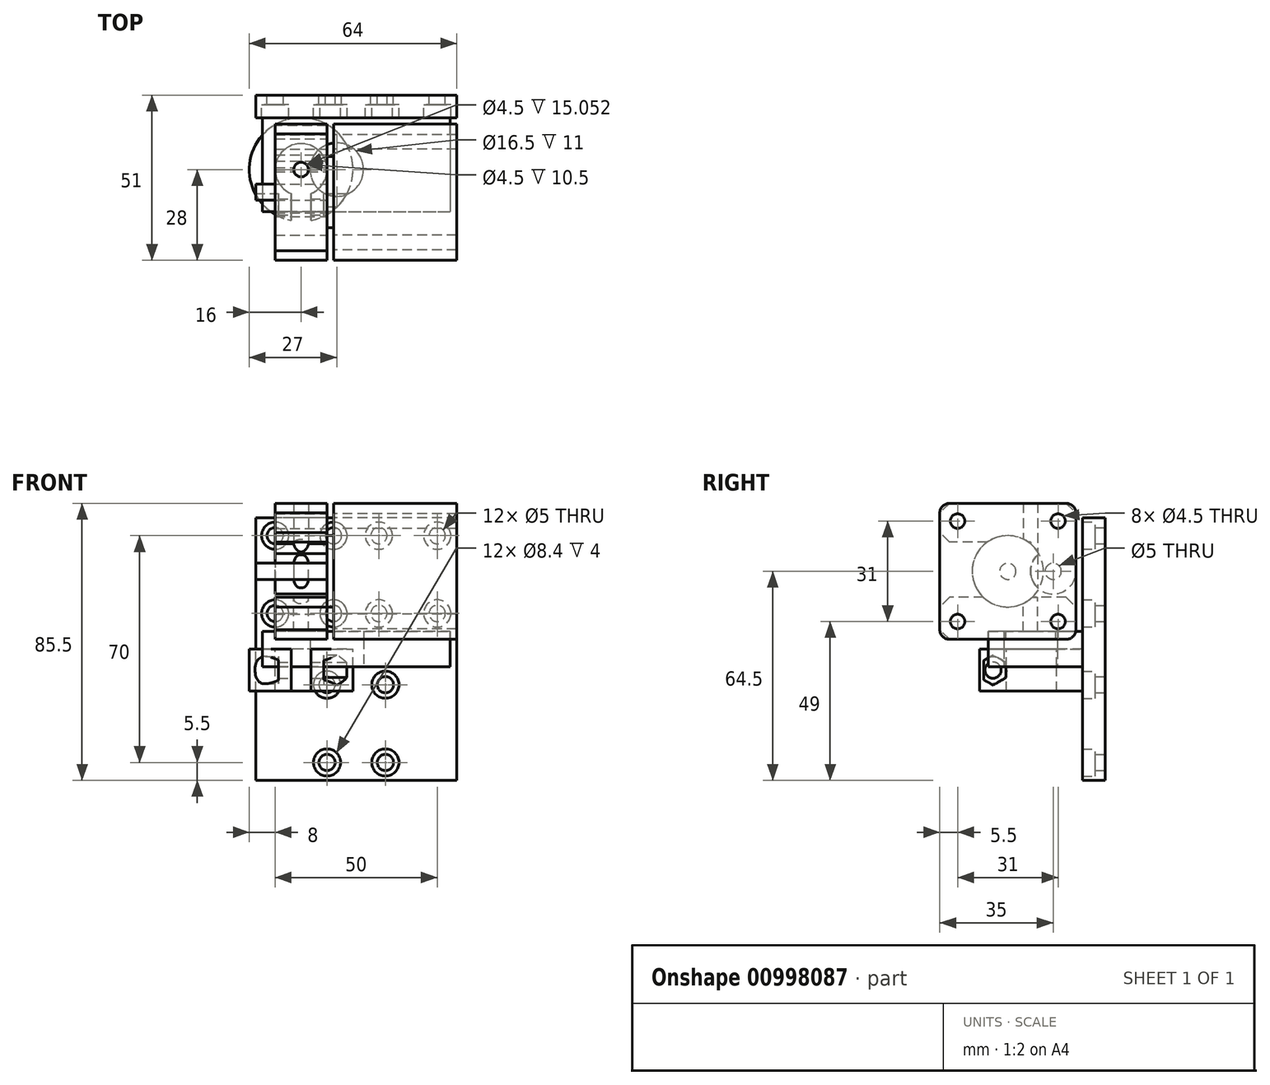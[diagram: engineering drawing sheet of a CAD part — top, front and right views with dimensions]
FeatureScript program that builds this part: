
annotation { "Feature Type Name" : "Feature", "Feature Type Description" : "" }
export const myFeature = defineFeature(function(context is Context, id is Id, definition is map)
    precondition{}
    {
        {
            var Q0;
            Q0=qCreatedBy(makeId("Front.planeOp"),FACE);
            var sketch = newSketch(context, id + "F0", { "sketchPlane" : qUnion([Q0])});
            skLineSegment(sketch, "E0.bottom", {"start": v(31, -40.5) * mm, "end": v(-31, -40.5) * mm});
            skLineSegment(sketch, "E0.top", {"start": v(31, 40.5) * mm, "end": v(-31, 40.5) * mm});
            skLineSegment(sketch, "E0.left", {"start": v(31, -40.5) * mm, "end": v(31, 40.5) * mm});
            skLineSegment(sketch, "E0.right", {"start": v(-31, -40.5) * mm, "end": v(-31, 40.5) * mm});
            skPoint(sketch, "E0.middle", {"position": v(0, 0) * mm});
            skLineSegment(sketch, "E1.bottom", {"start": v(-25, 35) * mm, "end": v(-7, 35) * mm, "construction": true});
            skLineSegment(sketch, "E1.top", {"start": v(-25, 11) * mm, "end": v(-7, 11) * mm, "construction": true});
            skLineSegment(sketch, "E1.left", {"start": v(-25, 35) * mm, "end": v(-25, 11) * mm, "construction": true});
            skLineSegment(sketch, "E1.right", {"start": v(-7, 35) * mm, "end": v(-7, 11) * mm, "construction": true});
            skLineSegment(sketch, "E2.bottom", {"start": v(-9, -11) * mm, "end": v(0, -11) * mm, "construction": true});
            skLineSegment(sketch, "E2.top", {"start": v(-9, -35) * mm, "end": v(0, -35) * mm, "construction": true});
            skLineSegment(sketch, "E2.left", {"start": v(-9, -11) * mm, "end": v(-9, -35) * mm, "construction": true});
            skLineSegment(sketch, "E3", {"start": v(0, 45.04) * mm, "end": v(0, -46.53) * mm, "construction": true});
            skCircle(sketch, "E4", {"center": v(-7, 11) * mm, "radius": 2.5 * mm});
            skCircle(sketch, "E5", {"center": v(-7, 35) * mm, "radius": 2.5 * mm});
            skCircle(sketch, "E6", {"center": v(-25, 35) * mm, "radius": 2.5 * mm});
            skCircle(sketch, "E7", {"center": v(-25, 11) * mm, "radius": 2.5 * mm});
            skCircle(sketch, "E8", {"center": v(-9, -11) * mm, "radius": 2.5 * mm});
            skCircle(sketch, "E9", {"center": v(-9, -35) * mm, "radius": 2.5 * mm});
            skCircle(sketch, "E10.MirrorC", {"center": v(7, 35) * mm, "radius": 2.5 * mm});
            skCircle(sketch, "E11.MirrorC", {"center": v(25, 35) * mm, "radius": 2.5 * mm});
            skCircle(sketch, "E12.MirrorC", {"center": v(25, 11) * mm, "radius": 2.5 * mm});
            skCircle(sketch, "E13.MirrorC", {"center": v(7, 11) * mm, "radius": 2.5 * mm});
            skCircle(sketch, "E14.MirrorC", {"center": v(9, -11) * mm, "radius": 2.5 * mm});
            skCircle(sketch, "E15.MirrorC", {"center": v(9, -35) * mm, "radius": 2.5 * mm});
            skSolve(sketch);
        }
        {
            var Q0;
            Q0 = qSketchRegion(id + "F0", true);
            extrude(context, id + "F1", {"entities" : qUnion([Q0]), "depth" : 3 * mm, "offsetDistance" : 25 * mm});
        }
        {
            var Q0;
            Q0=qCreatedBy(makeId("Top.planeOp"),FACE);
            var sketch = newSketch(context, id + "F2", { "sketchPlane" : qUnion([Q0])});
            skCircle(sketch, "E16", {"center": v(-17, -23) * mm, "radius": 8 * mm});
            skCircle(sketch, "E17", {"center": v(-17, -23) * mm, "radius": 16 * mm});
            skLineSegment(sketch, "E18", {"start": v(-17, 15.9) * mm, "end": v(-17, -56.42) * mm, "construction": true});
            skSolve(sketch);
        }
        {
            var Q0;
            Q0=qCreatedBy(makeId("Right.planeOp"),FACE);
            var Q1;
            Q1=sQuery(id+"F2.wireOp",VERTEX,"E16.center");
            cPlane(context, id + "F3", {"entities" : qUnion([Q0, Q1]), "cplaneType" : CPlaneType.PLANE_POINT, "offset" : 25 * mm, "width" : 150 * mm, "height" : 150 * mm});
        }
        {
            var Q0;
            Q0 = qSketchRegion(id + "F2", true);
            extrude(context, id + "F4", {"entities" : qUnion([Q0]), "oppositeDirection" : true, "depth" : 13 * mm, "offsetDistance" : 25 * mm});
        }
        {
            var Q0;
            Q0=makeQuery(id+"F4.opExtrude","CAP_FACE",FACE,{"disambiguationData":[OSD([sQuery(id+"F2.wireOp",EDGE,"E16"),sQuery(id+"F2.wireOp",EDGE,"E17")])],"isStart":true});
            var sketch = newSketch(context, id + "F5", { "sketchPlane" : qUnion([Q0])});
            skCircle(sketch, "E19.0", {"center": v(-17, -23) * mm, "radius": 16 * mm});
            skLineSegment(sketch, "E20.0", {"start": v(-17, 15.9) * mm, "end": v(-17, -56.42) * mm, "construction": true});
            skLineSegment(sketch, "E21", {"start": v(-20, -30.42) * mm, "end": v(-20, -38.72) * mm});
            skLineSegment(sketch, "E22.MirrorCS", {"start": v(-14, -30.42) * mm, "end": v(-14, -38.72) * mm});
            skCircle(sketch, "E23.0", {"center": v(-17, -23) * mm, "radius": 8 * mm});
            skSolve(sketch);
        }
        {
            var Q0;
            {var subQ0=sQuery(id+"F5.wireOp",EDGE,"E21");Q0=makeQuery(id+"F5.imprint","IMPRINT",FACE,{"disambiguationData":[TD([[makeQuery(id+"F5.imprint","IMPRINT",EDGE,{"derivedFrom":subQ0}),1.0]])]});}
            var Q1;
            Q1=makeQuery(id+"F4.opExtrude","CAP_FACE",FACE,{"disambiguationData":[OSD([sQuery(id+"F2.wireOp",EDGE,"E16"),sQuery(id+"F2.wireOp",EDGE,"E17")])],"isStart":false});
            extrude(context, id + "F6", {"entities" : qUnion([Q0]), "operationType" : NewBodyOperationType.REMOVE, "endBound" : BoundingType.UP_TO_SURFACE, "oppositeDirection" : true, "depth" : 25 * mm, "endBoundEntityFace" : qUnion([Q1]), "offsetDistance" : 25 * mm});
        }
        {
            var Q0;
            Q0=qCreatedBy(id+"F3.planeOp",FACE);
            var sketch = newSketch(context, id + "F7", { "sketchPlane" : qUnion([Q0])});
            skLineSegment(sketch, "E24.0.0", {"start": v(-38.72, -13) * mm, "end": v(-38.72, 0) * mm});
            skLineSegment(sketch, "E24.0.1", {"start": v(-38.72, 0) * mm, "end": v(-30.42, 0) * mm});
            skLineSegment(sketch, "E24.0.2", {"start": v(-30.42, 0) * mm, "end": v(-30.42, -13) * mm});
            skLineSegment(sketch, "E24.0.3", {"start": v(-30.42, -13) * mm, "end": v(-38.72, -13) * mm});
            skLineSegment(sketch, "E25", {"start": v(-30.42, 0) * mm, "end": v(-38.72, -13) * mm, "construction": true});
            skLineSegment(sketch, "E26", {"start": v(-38.72, 0) * mm, "end": v(-30.42, -13) * mm, "construction": true});
            skCircle(sketch, "E27", {"center": v(-34.57, -6.5) * mm, "radius": 2.5 * mm});
            skSolve(sketch);
        }
        {
            var Q0;
            Q0=makeQuery(id+"F7.imprint","IMPRINT",FACE,{"disambiguationData":[TD([[makeQuery(id+"F7.imprint","IMPRINT",EDGE,{"derivedFrom":sQuery(id+"F7.wireOp",EDGE,"E27")}),1.0]])]});
            extrude(context, id + "F8", {"entities" : qUnion([Q0]), "operationType" : NewBodyOperationType.REMOVE, "oppositeDirection" : true, "depth" : 14 * mm, "offsetDistance" : 25 * mm, "symmetric" : true});
        }
        {
            var Q0;
            Q0=makeQuery(id+"F8.boolean.opBoolean","COPY",FACE,{"derivedFrom":makeQuery(id+"F8.opExtrude","CAP_FACE",FACE,{"disambiguationData":[OSD([sQuery(id+"F7.wireOp",EDGE,"E27")])],"isStart":true})});
            var sketch = newSketch(context, id + "F9", { "sketchPlane" : qUnion([Q0])});
            skCircle(sketch, "E28.cCircle", {"center": v(34.57, -6.5) * mm, "radius": 4 * mm, "construction": true});
            skLineSegment(sketch, "E28.0", {"start": v(30.57, -8.8) * mm, "end": v(30.57, -4.2) * mm});
            skLineSegment(sketch, "E28.1", {"start": v(30.57, -4.2) * mm, "end": v(34.57, -1.88) * mm});
            skLineSegment(sketch, "E28.2", {"start": v(34.57, -1.88) * mm, "end": v(38.57, -4.2) * mm});
            skLineSegment(sketch, "E28.3", {"start": v(38.57, -4.2) * mm, "end": v(38.57, -8.8) * mm});
            skLineSegment(sketch, "E28.4", {"start": v(38.57, -8.8) * mm, "end": v(34.57, -11.12) * mm});
            skLineSegment(sketch, "E28.5", {"start": v(34.57, -11.12) * mm, "end": v(30.57, -8.8) * mm});
            skPoint(sketch, "E28.0.midPoint", {"position": v(30.57, -6.5) * mm});
            skCircle(sketch, "E29.0", {"center": v(34.57, -6.5) * mm, "radius": 2.5 * mm});
            skSolve(sketch);
        }
        {
            var Q0;
            Q0=makeQuery(id+"F9.imprint","IMPRINT",FACE,{"disambiguationData":[TD([[makeQuery(id+"F9.imprint","IMPRINT",EDGE,{"derivedFrom":sQuery(id+"F9.wireOp",EDGE,"E28.0")}),-1.0]])]});
            var Q1;
            Q1=makeQuery(id+"F9.imprint","IMPRINT",FACE,{"disambiguationData":[TD([[makeQuery(id+"F9.imprint","IMPRINT",EDGE,{"derivedFrom":sQuery(id+"F9.wireOp",EDGE,"E29.0")}),-1.0]])]});
            extrude(context, id + "F10", {"entities" : qUnion([Q0, Q1]), "operationType" : NewBodyOperationType.REMOVE, "oppositeDirection" : true, "depth" : 25 * mm, "offsetDistance" : 25 * mm});
        }
        {
            var Q0;
            Q0=makeQuery(id+"F8.boolean.opBoolean","COPY",FACE,{"derivedFrom":makeQuery(id+"F8.opExtrude","CAP_FACE",FACE,{"disambiguationData":[OSD([sQuery(id+"F7.wireOp",EDGE,"E27")])],"isStart":false})});
            var sketch = newSketch(context, id + "F11", { "sketchPlane" : qUnion([Q0])});
            skCircle(sketch, "E30", {"center": v(-34.57, -6.5) * mm, "radius": 4.2 * mm});
            skCircle(sketch, "E31.0", {"center": v(-34.57, -6.5) * mm, "radius": 2.5 * mm});
            skSolve(sketch);
        }
        {
            var Q0;
            Q0=makeQuery(id+"F11.imprint","IMPRINT",FACE,{"disambiguationData":[TD([[makeQuery(id+"F11.imprint","IMPRINT",EDGE,{"derivedFrom":sQuery(id+"F11.wireOp",EDGE,"E31.0")}),1.0]])]});
            var Q1;
            Q1=makeQuery(id+"F11.imprint","IMPRINT",FACE,{"disambiguationData":[TD([[makeQuery(id+"F11.imprint","IMPRINT",EDGE,{"derivedFrom":sQuery(id+"F11.wireOp",EDGE,"E30")}),1.0]])]});
            extrude(context, id + "F12", {"entities" : qUnion([Q0, Q1]), "operationType" : NewBodyOperationType.REMOVE, "oppositeDirection" : true, "depth" : 25 * mm, "offsetDistance" : 25 * mm});
        }
        {
            var Q0;
            Q0=qCreatedBy(makeId("Right.planeOp"),FACE);
            cPlane(context, id + "F13", {"entities" : qUnion([Q0]), "cplaneType" : CPlaneType.OFFSET, "offset" : 7 * mm, "oppositeDirection" : true, "width" : 150 * mm, "height" : 150 * mm});
        }
        {
            var Q0;
            Q0=qCreatedBy(id+"F13.planeOp",FACE);
            var sketch = newSketch(context, id + "F14", { "sketchPlane" : qUnion([Q0])});
            skLineSegment(sketch, "E32.bottom", {"start": v(-9, 3) * mm, "end": v(-51, 3) * mm});
            skLineSegment(sketch, "E32.top", {"start": v(-9, 45) * mm, "end": v(-51, 45) * mm});
            skLineSegment(sketch, "E32.left", {"start": v(-9, 3) * mm, "end": v(-9, 45) * mm});
            skLineSegment(sketch, "E32.right", {"start": v(-51, 3) * mm, "end": v(-51, 45) * mm});
            skLineSegment(sketch, "E33", {"start": v(-9, 45) * mm, "end": v(-51, 3) * mm, "construction": true});
            skLineSegment(sketch, "E34", {"start": v(-51, 45) * mm, "end": v(-9, 3) * mm, "construction": true});
            skCircle(sketch, "E35", {"center": v(-14.5, 39.5) * mm, "radius": 2.25 * mm});
            skLineSegment(sketch, "E36", {"start": v(-30, 45) * mm, "end": v(-30, 3) * mm, "construction": true});
            skLineSegment(sketch, "E37", {"start": v(-9, 24) * mm, "end": v(-51, 24) * mm, "construction": true});
            skCircle(sketch, "E38.MirrorC", {"center": v(-45.5, 39.5) * mm, "radius": 2.25 * mm});
            skCircle(sketch, "E39.MirrorC", {"center": v(-45.5, 8.5) * mm, "radius": 2.25 * mm});
            skCircle(sketch, "E40.MirrorC", {"center": v(-14.5, 8.5) * mm, "radius": 2.25 * mm});
            skSolve(sketch);
        }
        {
            var Q0;
            Q0=makeQuery(id+"F14.imprint","IMPRINT",FACE,{"disambiguationData":[TD([[makeQuery(id+"F14.imprint","IMPRINT",EDGE,{"derivedFrom":sQuery(id+"F14.wireOp",EDGE,"E32.bottom")}),-1.0]])]});
            extrude(context, id + "F15", {"entities" : qUnion([Q0]), "depth" : 38 * mm, "offsetDistance" : 25 * mm});
        }
        {
            var Q0;
            Q0=makeQuery(id+"F15.opExtrude","SWEPT_EDGE",EDGE,{"disambiguationData":[OSD([sQuery(id+"F14.wireOp",EDGE,"E32.top"),sQuery(id+"F14.wireOp",EDGE,"E32.left")])]});
            var Q1;
            Q1=makeQuery(id+"F15.opExtrude","SWEPT_EDGE",EDGE,{"disambiguationData":[OSD([sQuery(id+"F14.wireOp",EDGE,"E32.bottom"),sQuery(id+"F14.wireOp",EDGE,"E32.left")])]});
            var Q2;
            Q2=makeQuery(id+"F15.opExtrude","SWEPT_EDGE",EDGE,{"disambiguationData":[OSD([sQuery(id+"F14.wireOp",EDGE,"E32.top"),sQuery(id+"F14.wireOp",EDGE,"E32.right")])]});
            var Q3;
            Q3=makeQuery(id+"F15.opExtrude","SWEPT_EDGE",EDGE,{"disambiguationData":[OSD([sQuery(id+"F14.wireOp",EDGE,"E32.bottom"),sQuery(id+"F14.wireOp",EDGE,"E32.right")])]});
            fillet(context, id + "F16", {"entities" : qUnion([Q0, Q1, Q2, Q3]), "radius" : 3 * mm, "tangentPropagation" : true, "allowEdgeOverflow" : false});
        }
        {
            var Q0;
            Q0=makeQuery(id+"F15.opExtrude","CAP_FACE",FACE,{"disambiguationData":[OSD([sQuery(id+"F14.wireOp",EDGE,"E32.bottom"),sQuery(id+"F14.wireOp",EDGE,"E32.top"),sQuery(id+"F14.wireOp",EDGE,"E32.left"),sQuery(id+"F14.wireOp",EDGE,"E32.right"),sQuery(id+"F14.wireOp",EDGE,"E35"),sQuery(id+"F14.wireOp",EDGE,"E38.MirrorC"),sQuery(id+"F14.wireOp",EDGE,"E39.MirrorC"),sQuery(id+"F14.wireOp",EDGE,"E40.MirrorC")])],"isStart":true});
            var sketch = newSketch(context, id + "F17", { "sketchPlane" : qUnion([Q0])});
            skPoint(sketch, "E41.0", {"position": v(30, 24) * mm});
            skCircle(sketch, "E42", {"center": v(30, 24) * mm, "radius": 11 * mm});
            skSolve(sketch);
        }
        {
            var Q0;
            Q0=makeQuery(id+"F17.imprint","IMPRINT",FACE,{"disambiguationData":[TD([[makeQuery(id+"F17.imprint","IMPRINT",EDGE,{"derivedFrom":sQuery(id+"F17.wireOp",EDGE,"E42")}),1.0]])]});
            extrude(context, id + "F18", {"entities" : qUnion([Q0]), "operationType" : NewBodyOperationType.ADD, "depth" : 2 * mm, "offsetDistance" : 25 * mm});
        }
        {
            var Q0;
            Q0=makeQuery(id+"F18.opExtrude","CAP_FACE",FACE,{"disambiguationData":[OSD([sQuery(id+"F17.wireOp",EDGE,"E42")])],"isStart":false});
            var sketch = newSketch(context, id + "F19", { "sketchPlane" : qUnion([Q0])});
            skPoint(sketch, "E43.0", {"position": v(30, 24) * mm});
            skCircle(sketch, "E44", {"center": v(30, 24) * mm, "radius": 2.5 * mm});
            skSolve(sketch);
        }
        {
            var Q0;
            Q0 = qSketchRegion(id + "F19", true);
            extrude(context, id + "F20", {"entities" : qUnion([Q0]), "operationType" : NewBodyOperationType.ADD, "depth" : 22 * mm, "offsetDistance" : 25 * mm});
        }
        {
            var Q0;
            Q0=makeQuery(id+"F18.opExtrude","CAP_FACE",FACE,{"disambiguationData":[OSD([sQuery(id+"F17.wireOp",EDGE,"E42")])],"isStart":false});
            var sketch = newSketch(context, id + "F21", { "sketchPlane" : qUnion([Q0])});
            skCircle(sketch, "E45.0", {"center": v(14.5, 39.5) * mm, "radius": 2.25 * mm});
            skCircle(sketch, "E45.1", {"center": v(45.5, 39.5) * mm, "radius": 2.25 * mm});
            skCircle(sketch, "E45.2", {"center": v(45.5, 8.5) * mm, "radius": 2.25 * mm});
            skCircle(sketch, "E45.3", {"center": v(14.5, 8.5) * mm, "radius": 2.25 * mm});
            skCircle(sketch, "E46.0", {"center": v(30, 24) * mm, "radius": 2.5 * mm});
            skLineSegment(sketch, "E47.bottom", {"start": v(9, 45) * mm, "end": v(51, 45) * mm});
            skLineSegment(sketch, "E47.top", {"start": v(9, 33) * mm, "end": v(51, 33) * mm});
            skLineSegment(sketch, "E47.left", {"start": v(9, 45) * mm, "end": v(9, 33) * mm});
            skLineSegment(sketch, "E47.right", {"start": v(51, 45) * mm, "end": v(51, 33) * mm});
            skLineSegment(sketch, "E48.bottom", {"start": v(9, 16) * mm, "end": v(51, 16) * mm});
            skLineSegment(sketch, "E48.top", {"start": v(9, 3) * mm, "end": v(51, 3) * mm});
            skLineSegment(sketch, "E48.left", {"start": v(9, 16) * mm, "end": v(9, 3) * mm});
            skLineSegment(sketch, "E48.right", {"start": v(51, 16) * mm, "end": v(51, 3) * mm});
            skCircle(sketch, "E49", {"center": v(16, 24) * mm, "radius": 7 * mm});
            skLineSegment(sketch, "E50", {"start": v(9, 33) * mm, "end": v(9, 24) * mm});
            skLineSegment(sketch, "E51", {"start": v(23, 24) * mm, "end": v(23, 33) * mm});
            skLineSegment(sketch, "E52", {"start": v(9, 24) * mm, "end": v(23, 24) * mm, "construction": true});
            skCircle(sketch, "E53", {"center": v(16, 24) * mm, "radius": 2.5 * mm});
            skSolve(sketch);
        }
        {
            var Q0;
            Q0=makeQuery(id+"F21.imprint","IMPRINT",FACE,{"disambiguationData":[TD([[makeQuery(id+"F21.imprint","IMPRINT",EDGE,{"derivedFrom":sQuery(id+"F21.wireOp",EDGE,"E45.0")}),-1.0]])]});
            var Q1;
            Q1=makeQuery(id+"F21.imprint","IMPRINT",FACE,{"disambiguationData":[TD([[makeQuery(id+"F21.imprint","IMPRINT",EDGE,{"derivedFrom":sQuery(id+"F21.wireOp",EDGE,"E45.2")}),-1.0]])]});
            var Q2;
            {var subQ0=sQuery(id+"F21.wireOp",EDGE,"E49");var subQ1=makeQuery(id+"F21.imprint","INTERSECT",VERTEX,{"derivedFrom":[subQ0,sQuery(id+"F21.wireOp",EDGE,"E50")]});Q2=makeQuery(id+"F21.imprint","IMPRINT",FACE,{"disambiguationData":[TD([[makeQuery(id+"F21.imprint","IMPRINT",EDGE,{"disambiguationData":[TD([[subQ1,1.0]])],"derivedFrom":subQ0}),1.0]])]});}
            var Q3;
            {var subQ0=sQuery(id+"F21.wireOp",EDGE,"E49");var subQ1=makeQuery(id+"F21.imprint","INTERSECT",VERTEX,{"derivedFrom":[subQ0,sQuery(id+"F21.wireOp",EDGE,"E51")]});Q3=makeQuery(id+"F21.imprint","IMPRINT",FACE,{"disambiguationData":[TD([[makeQuery(id+"F21.imprint","IMPRINT",EDGE,{"disambiguationData":[TD([[subQ1,1.0]])],"derivedFrom":subQ0}),1.0]])]});}
            var Q4;
            {var subQ5=sQuery(id+"F21.wireOp",EDGE,"E50");Q4=makeQuery(id+"F21.imprint","IMPRINT",FACE,{"disambiguationData":[TD([[makeQuery(id+"F21.imprint","IMPRINT",EDGE,{"derivedFrom":subQ5}),1.0]])]});}
            extrude(context, id + "F22", {"entities" : qUnion([Q0, Q1, Q2, Q3, Q4]), "depth" : 16 * mm, "offsetDistance" : 25 * mm});
        }
        {
            var Q0;
            {var subQ0=sQuery(id+"F21.wireOp",EDGE,"E48.bottom");Q0=makeQuery(id+"F22.opExtrude","SWEPT_FACE",FACE,{"disambiguationData":[OSD([subQ0]),TDD([makeQuery(id+"F21.imprint","IMPRINT",EDGE,{"disambiguationData":[TD([[makeQuery(id+"F21.imprint","INTERSECT",VERTEX,{"derivedFrom":[subQ0,sQuery(id+"F21.wireOp",EDGE,"E48.left")]}),-1.0]])],"derivedFrom":subQ0})])]});}
            var sketch = newSketch(context, id + "F23", { "sketchPlane" : qUnion([Q0])});
            skCircle(sketch, "E54", {"center": v(-17, -23) * mm, "radius": 2.25 * mm});
            skLineSegment(sketch, "E55.0", {"start": v(-25, -9) * mm, "end": v(-9, -9) * mm});
            skPoint(sketch, "E56", {"position": v(-17, -9) * mm});
            skLineSegment(sketch, "E57", {"start": v(-17, -9) * mm, "end": v(-17, -38.9) * mm, "construction": true});
            skSolve(sketch);
        }
        {
            var Q0;
            {var subQ0=sQuery(id+"F23.wireOp",EDGE,"E54");var subQ1=sQuery(id+"F21.wireOp",EDGE,"E48.bottom");var subQ2=sQuery(id+"F17.wireOp",EDGE,"E42");var subQ3=makeQuery(id+"F22.opExtrude","SWEPT_EDGE",EDGE,{"disambiguationData":[OSD([subQ2,subQ1]),TDD([makeQuery(id+"F21.imprint","INTERSECT",VERTEX,{"disambiguationData":[OD(0.0)],"derivedFrom":[makeQuery(id+"F18.opExtrude","CAP_EDGE",EDGE,{"disambiguationData":[OSD([subQ2])],"isStart":false}),subQ1]})])]});var subQ4=makeQuery(id+"F23.imprint","INTERSECT",VERTEX,{"disambiguationData":[OD(0.0)],"derivedFrom":[subQ3,subQ0]});Q0=makeQuery(id+"F23.imprint","IMPRINT",FACE,{"disambiguationData":[TD([[makeQuery(id+"F23.imprint","IMPRINT",EDGE,{"disambiguationData":[TD([[subQ4,-1.0]])],"derivedFrom":subQ0}),1.0]])]});}
            var Q1;
            {var subQ0=sQuery(id+"F23.wireOp",EDGE,"E54");var subQ1=sQuery(id+"F21.wireOp",EDGE,"E48.bottom");var subQ2=sQuery(id+"F17.wireOp",EDGE,"E42");var subQ3=makeQuery(id+"F22.opExtrude","SWEPT_EDGE",EDGE,{"disambiguationData":[OSD([subQ2,subQ1]),TDD([makeQuery(id+"F21.imprint","INTERSECT",VERTEX,{"disambiguationData":[OD(0.0)],"derivedFrom":[makeQuery(id+"F18.opExtrude","CAP_EDGE",EDGE,{"disambiguationData":[OSD([subQ2])],"isStart":false}),subQ1]})])]});var subQ4=makeQuery(id+"F23.imprint","INTERSECT",VERTEX,{"disambiguationData":[OD(0.0)],"derivedFrom":[subQ3,subQ0]});Q1=makeQuery(id+"F23.imprint","IMPRINT",FACE,{"disambiguationData":[TD([[makeQuery(id+"F23.imprint","IMPRINT",EDGE,{"disambiguationData":[TD([[subQ4,1.0]])],"derivedFrom":subQ0}),1.0]])]});}
            var Q2;
            Q2=makeQuery(id+"F22.opExtrude","SWEPT_BODY",BODY,{"disambiguationData":[OSD([sQuery(id+"F17.wireOp",EDGE,"E42"),sQuery(id+"F21.wireOp",EDGE,"E45.2"),sQuery(id+"F21.wireOp",EDGE,"E45.3"),sQuery(id+"F21.wireOp",EDGE,"E48.bottom"),sQuery(id+"F21.wireOp",EDGE,"E48.top"),sQuery(id+"F21.wireOp",EDGE,"E48.left"),sQuery(id+"F21.wireOp",EDGE,"E48.right")])]});
            extrude(context, id + "F24", {"entities" : qUnion([Q0, Q1]), "operationType" : NewBodyOperationType.REMOVE, "endBound" : BoundingType.UP_TO_BODY, "oppositeDirection" : true, "depth" : 25 * mm, "endBoundEntityBody" : qUnion([Q2]), "offsetDistance" : 25 * mm});
        }
        {
            var Q0;
            Q0 = qSketchRegion(id + "F23", true);
            var Q1;
            Q1=makeQuery(id+"F22.opExtrude","SWEPT_FACE",FACE,{"disambiguationData":[OSD([sQuery(id+"F21.wireOp",EDGE,"E47.bottom")])]});
            var Q2;
            Q2=makeQuery(id+"F22.opExtrude","SWEPT_BODY",BODY,{"disambiguationData":[OSD([sQuery(id+"F17.wireOp",EDGE,"E42"),sQuery(id+"F21.wireOp",EDGE,"E45.0"),sQuery(id+"F21.wireOp",EDGE,"E45.1"),sQuery(id+"F21.wireOp",EDGE,"E47.bottom"),sQuery(id+"F21.wireOp",EDGE,"E47.top"),sQuery(id+"F21.wireOp",EDGE,"E47.left"),sQuery(id+"F21.wireOp",EDGE,"E47.right")])]});
            extrude(context, id + "F25", {"entities" : qUnion([Q0]), "operationType" : NewBodyOperationType.REMOVE, "endBound" : BoundingType.UP_TO_SURFACE, "depth" : 25 * mm, "endBoundEntityFace" : qUnion([Q1]), "endBoundEntityBody" : qUnion([Q2]), "offsetDistance" : 25 * mm});
        }
        {
            var Q0;
            Q0=makeQuery(id+"F22.opExtrude","SWEPT_EDGE",EDGE,{"disambiguationData":[OSD([sQuery(id+"F21.wireOp",EDGE,"E48.top"),sQuery(id+"F21.wireOp",EDGE,"E48.right")])]});
            var Q1;
            Q1=makeQuery(id+"F22.opExtrude","SWEPT_EDGE",EDGE,{"disambiguationData":[OSD([sQuery(id+"F21.wireOp",EDGE,"E48.top"),sQuery(id+"F21.wireOp",EDGE,"E48.left")])]});
            var Q2;
            Q2=makeQuery(id+"F22.opExtrude","SWEPT_EDGE",EDGE,{"disambiguationData":[OSD([sQuery(id+"F21.wireOp",EDGE,"E47.bottom"),sQuery(id+"F21.wireOp",EDGE,"E47.right")])]});
            var Q3;
            Q3=makeQuery(id+"F22.opExtrude","SWEPT_EDGE",EDGE,{"disambiguationData":[OSD([sQuery(id+"F21.wireOp",EDGE,"E47.bottom"),sQuery(id+"F21.wireOp",EDGE,"E47.left")])]});
            var Q4;
            Q4=makeQuery(id+"F22.opExtrude","SWEPT_EDGE",EDGE,{"disambiguationData":[OSD([sQuery(id+"F21.wireOp",EDGE,"E47.top"),sQuery(id+"F21.wireOp",EDGE,"E47.right")])]});
            var Q5;
            Q5=makeQuery(id+"F22.opExtrude","SWEPT_EDGE",EDGE,{"disambiguationData":[OSD([sQuery(id+"F21.wireOp",EDGE,"E48.bottom"),sQuery(id+"F21.wireOp",EDGE,"E48.right")])]});
            var Q6;
            Q6=makeQuery(id+"F22.opExtrude","SWEPT_EDGE",EDGE,{"disambiguationData":[OSD([sQuery(id+"F21.wireOp",EDGE,"E48.bottom"),sQuery(id+"F21.wireOp",EDGE,"E48.left")])]});
            chamfer(context, id + "F26", {"entities" : qUnion([Q0, Q1, Q2, Q3, Q4, Q5, Q6]), "width" : 3 * mm, "tangentPropagation" : true});
        }
        {
            var Q0;
            Q0=makeQuery(id+"F1.opExtrude","CAP_FACE",FACE,{"disambiguationData":[OSD([sQuery(id+"F0.wireOp",EDGE,"E0.bottom"),sQuery(id+"F0.wireOp",EDGE,"E0.top"),sQuery(id+"F0.wireOp",EDGE,"E0.left"),sQuery(id+"F0.wireOp",EDGE,"E0.right"),sQuery(id+"F0.wireOp",EDGE,"E4"),sQuery(id+"F0.wireOp",EDGE,"E5"),sQuery(id+"F0.wireOp",EDGE,"E6"),sQuery(id+"F0.wireOp",EDGE,"E7"),sQuery(id+"F0.wireOp",EDGE,"E8"),sQuery(id+"F0.wireOp",EDGE,"E9"),sQuery(id+"F0.wireOp",EDGE,"E10.MirrorC"),sQuery(id+"F0.wireOp",EDGE,"E11.MirrorC"),sQuery(id+"F0.wireOp",EDGE,"E12.MirrorC"),sQuery(id+"F0.wireOp",EDGE,"E13.MirrorC"),sQuery(id+"F0.wireOp",EDGE,"E14.MirrorC"),sQuery(id+"F0.wireOp",EDGE,"E15.MirrorC")])],"isStart":false});
            var sketch = newSketch(context, id + "F27", { "sketchPlane" : qUnion([Q0])});
            skCircle(sketch, "E58.0", {"center": v(-9, -11) * mm, "radius": 2.5 * mm});
            skCircle(sketch, "E58.1", {"center": v(9, -11) * mm, "radius": 2.5 * mm});
            skCircle(sketch, "E58.2", {"center": v(-9, -35) * mm, "radius": 2.5 * mm});
            skCircle(sketch, "E58.3", {"center": v(9, -35) * mm, "radius": 2.5 * mm});
            skLineSegment(sketch, "E58.4", {"start": v(-31, -40.5) * mm, "end": v(-31, 40.5) * mm});
            skLineSegment(sketch, "E58.5", {"start": v(31, -40.5) * mm, "end": v(-31, -40.5) * mm});
            skLineSegment(sketch, "E58.6", {"start": v(31, -40.5) * mm, "end": v(31, 40.5) * mm});
            skLineSegment(sketch, "E58.7", {"start": v(31, 40.5) * mm, "end": v(-31, 40.5) * mm});
            skCircle(sketch, "E58.8", {"center": v(-25, 35) * mm, "radius": 2.5 * mm});
            skCircle(sketch, "E58.9", {"center": v(-25, 11) * mm, "radius": 2.5 * mm});
            skCircle(sketch, "E58.10", {"center": v(-7, 35) * mm, "radius": 2.5 * mm});
            skCircle(sketch, "E58.11", {"center": v(-7, 11) * mm, "radius": 2.5 * mm});
            skCircle(sketch, "E58.12", {"center": v(7, 11) * mm, "radius": 2.5 * mm});
            skCircle(sketch, "E58.13", {"center": v(7, 35) * mm, "radius": 2.5 * mm});
            skCircle(sketch, "E58.14", {"center": v(25, 35) * mm, "radius": 2.5 * mm});
            skCircle(sketch, "E58.15", {"center": v(25, 11) * mm, "radius": 2.5 * mm});
            skCircle(sketch, "E59.0", {"center": v(-25, 35) * mm, "radius": 4.2 * mm});
            skLineSegment(sketch, "E60.0", {"start": v(0, 45.04) * mm, "end": v(0, -46.53) * mm, "construction": true});
            skCircle(sketch, "E61.0", {"center": v(-7, 35) * mm, "radius": 4.2 * mm});
            skCircle(sketch, "E62.0", {"center": v(-7, 11) * mm, "radius": 4.2 * mm});
            skCircle(sketch, "E63.0", {"center": v(-25, 11) * mm, "radius": 4.2 * mm});
            skCircle(sketch, "E64.0", {"center": v(-9, -11) * mm, "radius": 4.2 * mm});
            skCircle(sketch, "E65.0", {"center": v(-9, -35) * mm, "radius": 4.2 * mm});
            skCircle(sketch, "E66.MirrorC", {"center": v(9, -35) * mm, "radius": 4.2 * mm});
            skCircle(sketch, "E67.MirrorC", {"center": v(9, -11) * mm, "radius": 4.2 * mm});
            skCircle(sketch, "E68.MirrorC", {"center": v(7, 11) * mm, "radius": 4.2 * mm});
            skCircle(sketch, "E69.MirrorC", {"center": v(25, 11) * mm, "radius": 4.2 * mm});
            skCircle(sketch, "E70.MirrorC", {"center": v(7, 35) * mm, "radius": 4.2 * mm});
            skCircle(sketch, "E71.MirrorC", {"center": v(25, 35) * mm, "radius": 4.2 * mm});
            skSolve(sketch);
        }
        {
            var Q0;
            Q0=makeQuery(id+"F27.imprint","IMPRINT",FACE,{"disambiguationData":[TD([[makeQuery(id+"F27.imprint","IMPRINT",EDGE,{"derivedFrom":sQuery(id+"F27.wireOp",EDGE,"E58.4")}),-1.0]])]});
            extrude(context, id + "F28", {"entities" : qUnion([Q0]), "depth" : 4 * mm, "offsetDistance" : 25 * mm});
        }
        {
            var Q0;
            Q0=qCreatedBy(makeId("Top.planeOp"),FACE);
            var sketch = newSketch(context, id + "F29", { "sketchPlane" : qUnion([Q0])});
            skLineSegment(sketch, "E72.bottom", {"start": v(-29, -3) * mm, "end": v(29, -3) * mm});
            skLineSegment(sketch, "E72.top", {"start": v(-29, -36) * mm, "end": v(29, -36) * mm});
            skLineSegment(sketch, "E72.left", {"start": v(-29, -3) * mm, "end": v(-29, -36) * mm});
            skLineSegment(sketch, "E72.right", {"start": v(29, -3) * mm, "end": v(29, -36) * mm});
            skLineSegment(sketch, "E73", {"start": v(-29, -3) * mm, "end": v(29, -36) * mm, "construction": true});
            skLineSegment(sketch, "E74", {"start": v(29, -3) * mm, "end": v(-29, -36) * mm, "construction": true});
            skLineSegment(sketch, "E75", {"start": v(0, 15.37) * mm, "end": v(0, -43.59) * mm, "construction": true});
            skPoint(sketch, "E76", {"position": v(0, -19.5) * mm});
            skCircle(sketch, "E77", {"center": v(-6, -23) * mm, "radius": 8.25 * mm});
            skLineSegment(sketch, "E78.bottom", {"start": v(-17, -36) * mm, "end": v(5, -36) * mm});
            skLineSegment(sketch, "E78.top", {"start": v(-17, -3) * mm, "end": v(5, -3) * mm});
            skLineSegment(sketch, "E78.left", {"start": v(-17, -36) * mm, "end": v(-17, -3) * mm});
            skLineSegment(sketch, "E78.right", {"start": v(5, -36) * mm, "end": v(5, -3) * mm});
            skLineSegment(sketch, "E79", {"start": v(-6, -3) * mm, "end": v(-6, -36) * mm, "construction": true});
            skPoint(sketch, "E80.endSnap0", {"position": v(-29, -19.5) * mm});
            skSolve(sketch);
        }
        {
            var Q0;
            {var subQ1=sQuery(id+"F29.wireOp",EDGE,"E72.bottom");Q0=makeQuery(id+"F29.imprint","IMPRINT",FACE,{"disambiguationData":[TD([[makeQuery(id+"F29.imprint","IMPRINT",EDGE,{"derivedFrom":subQ1}),-1.0]])]});}
            var Q1;
            Q1=makeQuery(id+"F29.imprint","IMPRINT",FACE,{"disambiguationData":[TD([[makeQuery(id+"F29.imprint","IMPRINT",EDGE,{"derivedFrom":sQuery(id+"F29.wireOp",EDGE,"E77")}),-1.0]])]});
            extrude(context, id + "F30", {"entities" : qUnion([Q0, Q1]), "operationType" : NewBodyOperationType.ADD, "depth" : 11 * mm, "offsetDistance" : 25 * mm, "symmetric" : true});
        }
    });
